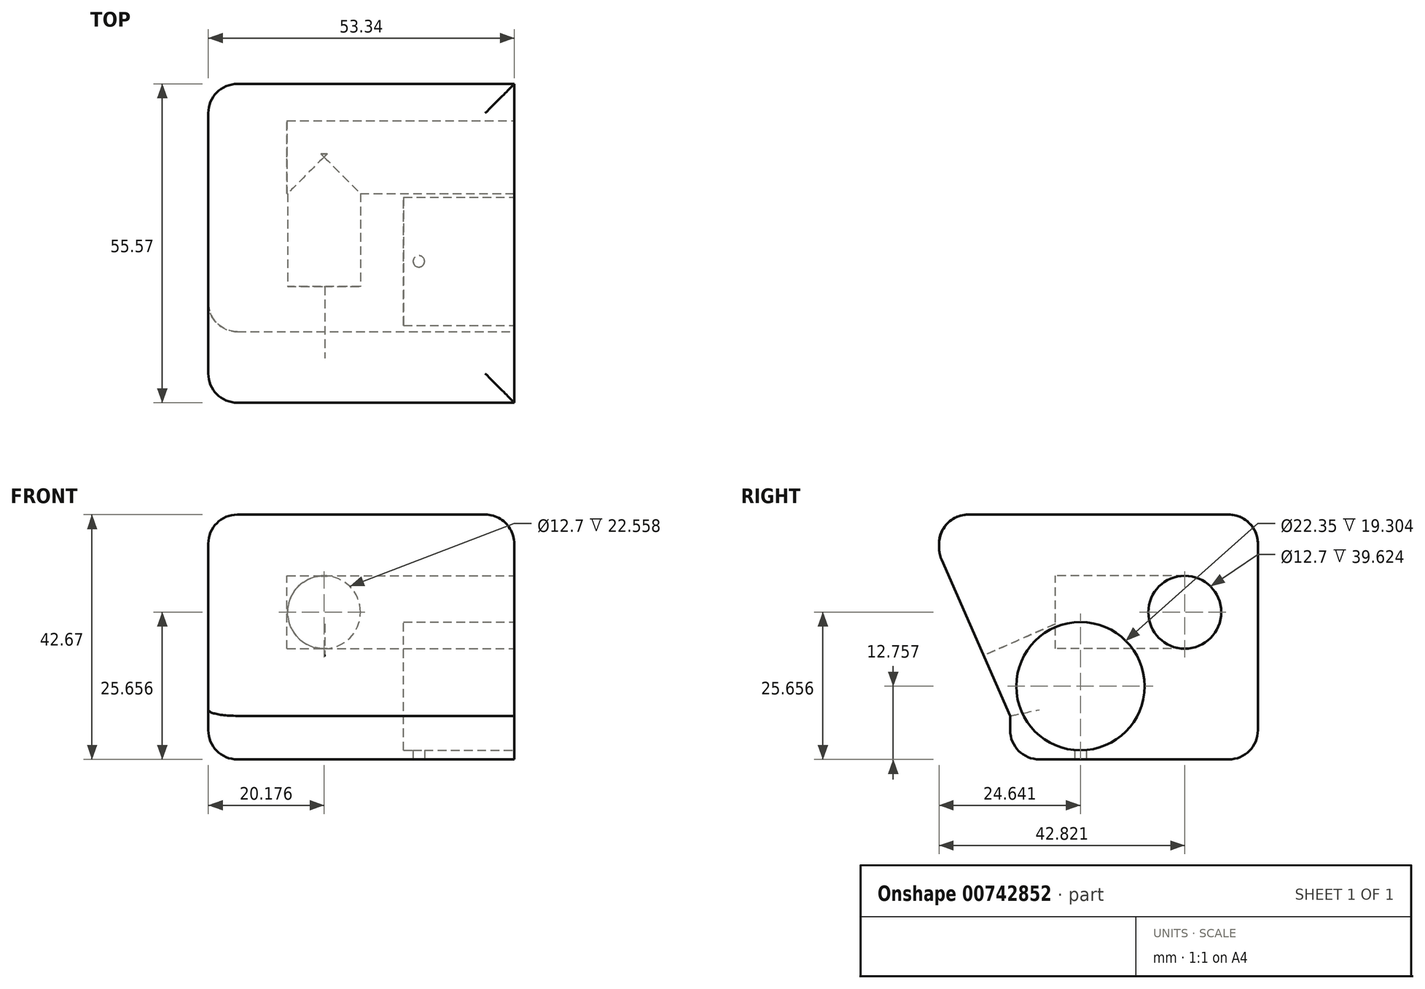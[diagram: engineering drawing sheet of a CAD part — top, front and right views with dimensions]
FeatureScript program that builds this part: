
annotation { "Feature Type Name" : "Feature", "Feature Type Description" : "" }
export const myFeature = defineFeature(function(context is Context, id is Id, definition is map)
    precondition{}
    {
        {
            var Q0;
            Q0=qCreatedBy(makeId("Top.planeOp"),FACE);
            var sketch = newSketch(context, id + "F0", { "sketchPlane" : qUnion([Q0])});
            skLineSegment(sketch, "E0.bottom", {"start": v(-76.1, -17.91) * mm, "end": v(-22.76, -17.91) * mm});
            skLineSegment(sketch, "E0.top", {"start": v(-76.1, -61.1) * mm, "end": v(-22.76, -61.1) * mm});
            skLineSegment(sketch, "E0.left", {"start": v(-76.1, -17.91) * mm, "end": v(-76.1, -61.1) * mm});
            skLineSegment(sketch, "E0.right", {"start": v(-22.76, -17.91) * mm, "end": v(-22.76, -61.1) * mm});
            skSolve(sketch);
        }
        {
            var Q0;
            Q0=makeQuery(id+"F0.imprint","IMPRINT",FACE,{"disambiguationData":[TD([[makeQuery(id+"F0.imprint","IMPRINT",EDGE,{"derivedFrom":sQuery(id+"F0.wireOp",EDGE,"E0.bottom")}),-1.0]])]});
            extrude(context, id + "F1", {"entities" : qUnion([Q0]), "depth" : 35.81 * mm, "offsetDistance" : 25.4 * mm});
        }
        {
            var Q0;
            Q0=makeQuery(id+"F1.opExtrude","SWEPT_FACE",FACE,{"disambiguationData":[OSD([sQuery(id+"F0.wireOp",EDGE,"E0.left")])]});
            var sketch = newSketch(context, id + "F2", { "sketchPlane" : qUnion([Q0])});
            skLineSegment(sketch, "E1", {"start": v(61.1, 35.81) * mm, "end": v(73.48, 35.81) * mm});
            skLineSegment(sketch, "E2", {"start": v(73.48, 35.81) * mm, "end": v(61.1, 7.59) * mm});
            skLineSegment(sketch, "E3", {"start": v(61.1, 7.59) * mm, "end": v(61.1, 35.81) * mm});
            skSolve(sketch);
        }
        {
            var Q0;
            Q0 = qSketchRegion(id + "F2", true);
            var Q1;
            Q1=makeQuery(id+"F1.opExtrude","SWEPT_FACE",FACE,{"disambiguationData":[OSD([sQuery(id+"F0.wireOp",EDGE,"E0.right")])]});
            extrude(context, id + "F3", {"entities" : qUnion([Q0]), "operationType" : NewBodyOperationType.ADD, "endBound" : BoundingType.UP_TO_SURFACE, "oppositeDirection" : true, "depth" : 23.1 * mm, "endBoundEntityFace" : qUnion([Q1]), "offsetDistance" : 25.4 * mm});
        }
        {
            var Q0;
            Q0=makeQuery(id+"F3.opExtrude","SWEPT_FACE",FACE,{"disambiguationData":[OSD([sQuery(id+"F2.wireOp",EDGE,"E2")])]});
            var sketch = newSketch(context, id + "F4", { "sketchPlane" : qUnion([Q0])});
            skPoint(sketch, "E4", {"position": v(-55.78, 42.99) * mm});
            skSolve(sketch);
        }
        {
            var Q0;
            Q0=sQuery(id+"F4.wireOp",VERTEX,"E4");
            var Q1;
            Q1=makeQuery(id+"F1.opExtrude","SWEPT_BODY",BODY,{"disambiguationData":[OSD([sQuery(id+"F0.wireOp",EDGE,"E0.bottom"),sQuery(id+"F0.wireOp",EDGE,"E0.top"),sQuery(id+"F0.wireOp",EDGE,"E0.left"),sQuery(id+"F0.wireOp",EDGE,"E0.right")])]});
            hole(context, id + "F5", {"style" : HoleStyle.SIMPLE, "endStyle" : HoleEndStyle.BLIND, "standardTappedOrClearance" : lookupTablePath({ "standard" : "ANSI", "size" : "3/4 (0.75)", "type" : "Drilled" }), "standardBlindInLast" : lookupTablePath({ "standard" : "ANSI", "size" : "3/4", "type" : "Drilled" }), "holeDiameter" : 3 / 101.6 * mm, "majorDiameter" : 19.05 * mm, "holeDepth" : 20.32 * mm, "isTappedThrough" : true, "tappedDepth" : 12.7 * mm, "tapClearance" : 3, "locations" : qUnion([Q0]), "scope" : qUnion([Q1])});
        }
        {
            var Q0;
            {var subQ0=sQuery(id+"F0.wireOp",EDGE,"E0.right");Q0=makeQuery(id+"F3.boolean.opBoolean","MERGE",FACE,{"derivedFrom":[makeQuery(id+"F1.opExtrude","SWEPT_FACE",FACE,{"disambiguationData":[OSD([subQ0])]}),makeQuery(id+"F3.opExtrude","CAP_FACE",FACE,{"disambiguationData":[OSD([subQ0])],"isStart":false})]});}
            var sketch = newSketch(context, id + "F6", { "sketchPlane" : qUnion([Q0])});
            skCircle(sketch, "E5", {"center": v(-48.84, 12.76) * mm, "radius": 11.18 * mm});
            skPoint(sketch, "E5.centerSnap0", {"position": v(-39.5, 0) * mm});
            skPoint(sketch, "E6", {"position": v(-30.66, 25.66) * mm});
            skSolve(sketch);
        }
        {
            var Q0;
            Q0 = qSketchRegion(id + "F6", true);
            extrude(context, id + "F7", {"entities" : qUnion([Q0]), "operationType" : NewBodyOperationType.REMOVE, "oppositeDirection" : true, "depth" : 19.3 * mm, "offsetDistance" : 25.4 * mm});
        }
        {
            var Q0;
            Q0=makeQuery(id+"F1.opExtrude","SWEPT_FACE",FACE,{"disambiguationData":[OSD([sQuery(id+"F0.wireOp",EDGE,"E0.top")])]});
            var sketch = newSketch(context, id + "F8", { "sketchPlane" : qUnion([Q0])});
            skPoint(sketch, "E7", {"position": v(-43.82, 27.76) * mm});
            skSolve(sketch);
        }
        {
            var Q0;
            Q0=sQuery(id+"F6.wireOp",VERTEX,"E6");
            var Q1;
            Q1=makeQuery(id+"F1.opExtrude","SWEPT_BODY",BODY,{"disambiguationData":[OSD([sQuery(id+"F0.wireOp",EDGE,"E0.bottom"),sQuery(id+"F0.wireOp",EDGE,"E0.top"),sQuery(id+"F0.wireOp",EDGE,"E0.left"),sQuery(id+"F0.wireOp",EDGE,"E0.right")])]});
            hole(context, id + "F9", {"style" : HoleStyle.SIMPLE, "endStyle" : HoleEndStyle.BLIND, "standardTappedOrClearance" : lookupTablePath({ "standard" : "ANSI", "size" : "3/4 (0.75)", "type" : "Drilled" }), "standardBlindInLast" : lookupTablePath({ "standard" : "ANSI", "size" : "3/4", "type" : "Drilled" }), "holeDiameter" : 3 / 101.6 * mm, "majorDiameter" : 12.7 * mm, "holeDepth" : 18.56 * mm, "isTappedThrough" : true, "tappedDepth" : 12.7 * mm, "tapClearance" : 3, "locations" : qUnion([Q0]), "scope" : qUnion([Q1])});
        }
        {
            var Q0;
            Q0=makeQuery(id+"F6.imprint","IMPRINT",FACE,{"disambiguationData":[TD([[makeQuery(id+"F6.imprint","IMPRINT",EDGE,{"derivedFrom":sQuery(id+"F6.wireOp",EDGE,"E5")}),-1.0]])]});
            var sketch = newSketch(context, id + "F10", { "sketchPlane" : qUnion([Q0])});
            skCircle(sketch, "E8", {"center": v(-30.66, 25.66) * mm, "radius": 6.35 * mm});
            skSolve(sketch);
        }
        {
            var Q0;
            Q0 = qSketchRegion(id + "F10", true);
            extrude(context, id + "F11", {"entities" : qUnion([Q0]), "operationType" : NewBodyOperationType.REMOVE, "oppositeDirection" : true, "depth" : 39.62 * mm, "offsetDistance" : 25.4 * mm});
        }
        {
            var Q0;
            {var subQ0=sQuery(id+"F0.wireOp",EDGE,"E0.top");Q0=makeQuery(id+"F8.imprint","IMPRINT",FACE,{"disambiguationData":[TD([[makeQuery(id+"F8.imprint","IMPRINT",EDGE,{"derivedFrom":makeQuery(id+"F1.opExtrude","CAP_EDGE",EDGE,{"disambiguationData":[OSD([subQ0])],"isStart":true})}),1.0]])]});}
            var sketch = newSketch(context, id + "F12", { "sketchPlane" : qUnion([Q0])});
            skCircle(sketch, "E9", {"center": v(-55.92, 25.66) * mm, "radius": 6.35 * mm});
            skSolve(sketch);
        }
        {
            var Q0;
            Q0=makeQuery(id+"F12.imprint","IMPRINT",FACE,{"disambiguationData":[TD([[makeQuery(id+"F12.imprint","IMPRINT",EDGE,{"derivedFrom":sQuery(id+"F12.wireOp",EDGE,"E9")}),1.0]])]});
            extrude(context, id + "F13", {"entities" : qUnion([Q0]), "operationType" : NewBodyOperationType.REMOVE, "oppositeDirection" : true, "depth" : 30.99 * mm, "offsetDistance" : 25.4 * mm, "hasSecondDirection" : true, "secondDirectionOppositeDirection" : true, "secondDirectionDepth" : 7.87 * mm});
        }
        {
            var Q0;
            Q0=makeQuery(id+"F1.opExtrude","CAP_FACE",FACE,{"disambiguationData":[OSD([sQuery(id+"F0.wireOp",EDGE,"E0.bottom"),sQuery(id+"F0.wireOp",EDGE,"E0.top"),sQuery(id+"F0.wireOp",EDGE,"E0.left"),sQuery(id+"F0.wireOp",EDGE,"E0.right")])],"isStart":true});
            var sketch = newSketch(context, id + "F14", { "sketchPlane" : qUnion([Q0])});
            skPoint(sketch, "E10", {"position": v(-39.4, 48.84) * mm});
            skSolve(sketch);
        }
        {
            var Q0;
            Q0=sQuery(id+"F14.wireOp",VERTEX,"E10");
            var Q1;
            Q1=makeQuery(id+"F1.opExtrude","SWEPT_BODY",BODY,{"disambiguationData":[OSD([sQuery(id+"F0.wireOp",EDGE,"E0.bottom"),sQuery(id+"F0.wireOp",EDGE,"E0.top"),sQuery(id+"F0.wireOp",EDGE,"E0.left"),sQuery(id+"F0.wireOp",EDGE,"E0.right")])]});
            hole(context, id + "F15", {"style" : HoleStyle.SIMPLE, "endStyle" : HoleEndStyle.BLIND, "standardTappedOrClearance" : lookupTablePath({ "standard" : "ANSI", "engagement" : "75%", "pitch" : "48 tpi", "size" : "#3", "type" : "Tapped" }), "standardBlindInLast" : lookupTablePath({ "standard" : "ANSI", "engagement" : "75%", "pitch" : "48 tpi", "size" : "#3", "type" : "Tapped" }), "holeDiameter" : 2 * mm, "majorDiameter" : 2.5 * mm, "showTappedDepth" : true, "holeDepth" : 14.29 * mm, "isTappedThrough" : true, "tappedDepth" : 12.7 * mm, "tapClearance" : 3, "locations" : qUnion([Q0]), "scope" : qUnion([Q1])});
        }
        {
            var Q0;
            Q0=makeQuery(id+"F3.boolean.opBoolean","MERGE",FACE,{"derivedFrom":[makeQuery(id+"F1.opExtrude","CAP_FACE",FACE,{"disambiguationData":[OSD([sQuery(id+"F0.wireOp",EDGE,"E0.bottom"),sQuery(id+"F0.wireOp",EDGE,"E0.top"),sQuery(id+"F0.wireOp",EDGE,"E0.left"),sQuery(id+"F0.wireOp",EDGE,"E0.right")])],"isStart":false}),makeQuery(id+"F3.opExtrude","SWEPT_FACE",FACE,{"disambiguationData":[OSD([sQuery(id+"F2.wireOp",EDGE,"E1")])]})]});
            extrude(context, id + "F16", {"entities" : qUnion([Q0]), "operationType" : NewBodyOperationType.ADD, "depth" : 6.86 * mm, "offsetDistance" : 25.4 * mm});
        }
        {
            var Q0;
            Q0=makeQuery(id+"F16.opExtrude","CAP_EDGE",EDGE,{"disambiguationData":[OSD([sQuery(id+"F0.wireOp",EDGE,"E0.left"),sQuery(id+"F2.wireOp",EDGE,"E1")])],"isStart":false});
            var Q1;
            Q1=makeQuery(id+"F16.opExtrude","CAP_EDGE",EDGE,{"disambiguationData":[OSD([sQuery(id+"F2.wireOp",EDGE,"E1"),sQuery(id+"F2.wireOp",EDGE,"E2")])],"isStart":false});
            var Q2;
            Q2=makeQuery(id+"F16.opExtrude","CAP_EDGE",EDGE,{"disambiguationData":[OSD([sQuery(id+"F0.wireOp",EDGE,"E0.right"),sQuery(id+"F2.wireOp",EDGE,"E1")])],"isStart":false});
            var Q3;
            Q3=makeQuery(id+"F16.opExtrude","CAP_EDGE",EDGE,{"disambiguationData":[OSD([sQuery(id+"F0.wireOp",EDGE,"E0.bottom")])],"isStart":false});
            var Q4;
            Q4=makeQuery(id+"F3.opExtrude","CAP_EDGE",EDGE,{"disambiguationData":[OSD([sQuery(id+"F2.wireOp",EDGE,"E2")])],"isStart":true});
            var Q5;
            Q5=makeQuery(id+"F1.opExtrude","SWEPT_EDGE",EDGE,{"disambiguationData":[OSD([sQuery(id+"F0.wireOp",EDGE,"E0.top"),sQuery(id+"F0.wireOp",EDGE,"E0.left")])]});
            var Q6;
            {var subQ0=sQuery(id+"F2.wireOp",EDGE,"E1");var subQ1=sQuery(id+"F0.wireOp",EDGE,"E0.left");Q6=makeQuery(id+"F16.boolean.opBoolean","MERGE",FACE,{"derivedFrom":[makeQuery(id+"F3.boolean.opBoolean","MERGE",FACE,{"derivedFrom":[makeQuery(id+"F1.opExtrude","SWEPT_FACE",FACE,{"disambiguationData":[OSD([subQ1])]}),makeQuery(id+"F3.opExtrude","CAP_FACE",FACE,{"disambiguationData":[OSD([subQ0,sQuery(id+"F2.wireOp",EDGE,"E2"),sQuery(id+"F2.wireOp",EDGE,"E3")])],"isStart":true})]}),makeQuery(id+"F16.opExtrude","SWEPT_FACE",FACE,{"disambiguationData":[OSD([subQ1,subQ0])]})]});}
            var Q7;
            Q7=makeQuery(id+"F1.opExtrude","CAP_EDGE",EDGE,{"disambiguationData":[OSD([sQuery(id+"F0.wireOp",EDGE,"E0.top")])],"isStart":true});
            var Q8;
            {var subQ0=sQuery(id+"F2.wireOp",EDGE,"E2");var subQ1=sQuery(id+"F2.wireOp",EDGE,"E1");Q8=makeQuery(id+"F16.boolean.opBoolean","MERGE",EDGE,{"derivedFrom":[makeQuery(id+"F3.opExtrude","SWEPT_EDGE",EDGE,{"disambiguationData":[OSD([subQ1,subQ0])]}),makeQuery(id+"F16.opExtrude","CAP_EDGE",EDGE,{"disambiguationData":[OSD([subQ1,subQ0])],"isStart":true})]});}
            var Q9;
            Q9=makeQuery(id+"F3.opExtrude","SWEPT_EDGE",EDGE,{"disambiguationData":[OSD([sQuery(id+"F0.wireOp",EDGE,"E0.top"),sQuery(id+"F0.wireOp",EDGE,"E0.left"),sQuery(id+"F2.wireOp",EDGE,"E2"),sQuery(id+"F2.wireOp",EDGE,"E3")])]});
            fillet(context, id + "F17", {"entities" : qUnion([Q0, Q1, Q2, Q3, Q4, Q5, Q6, Q7, Q8, Q9]), "radius" : 5.08 * mm, "tangentPropagation" : true, "allowEdgeOverflow" : false});
        }
        {
            var Q0;
            Q0=makeQuery(id+"F1.opExtrude","CAP_EDGE",EDGE,{"disambiguationData":[OSD([sQuery(id+"F0.wireOp",EDGE,"E0.bottom")])],"isStart":true});
            fillet(context, id + "F18", {"entities" : qUnion([Q0]), "radius" : 5.08 * mm, "tangentPropagation" : true, "allowEdgeOverflow" : false});
        }
    });
